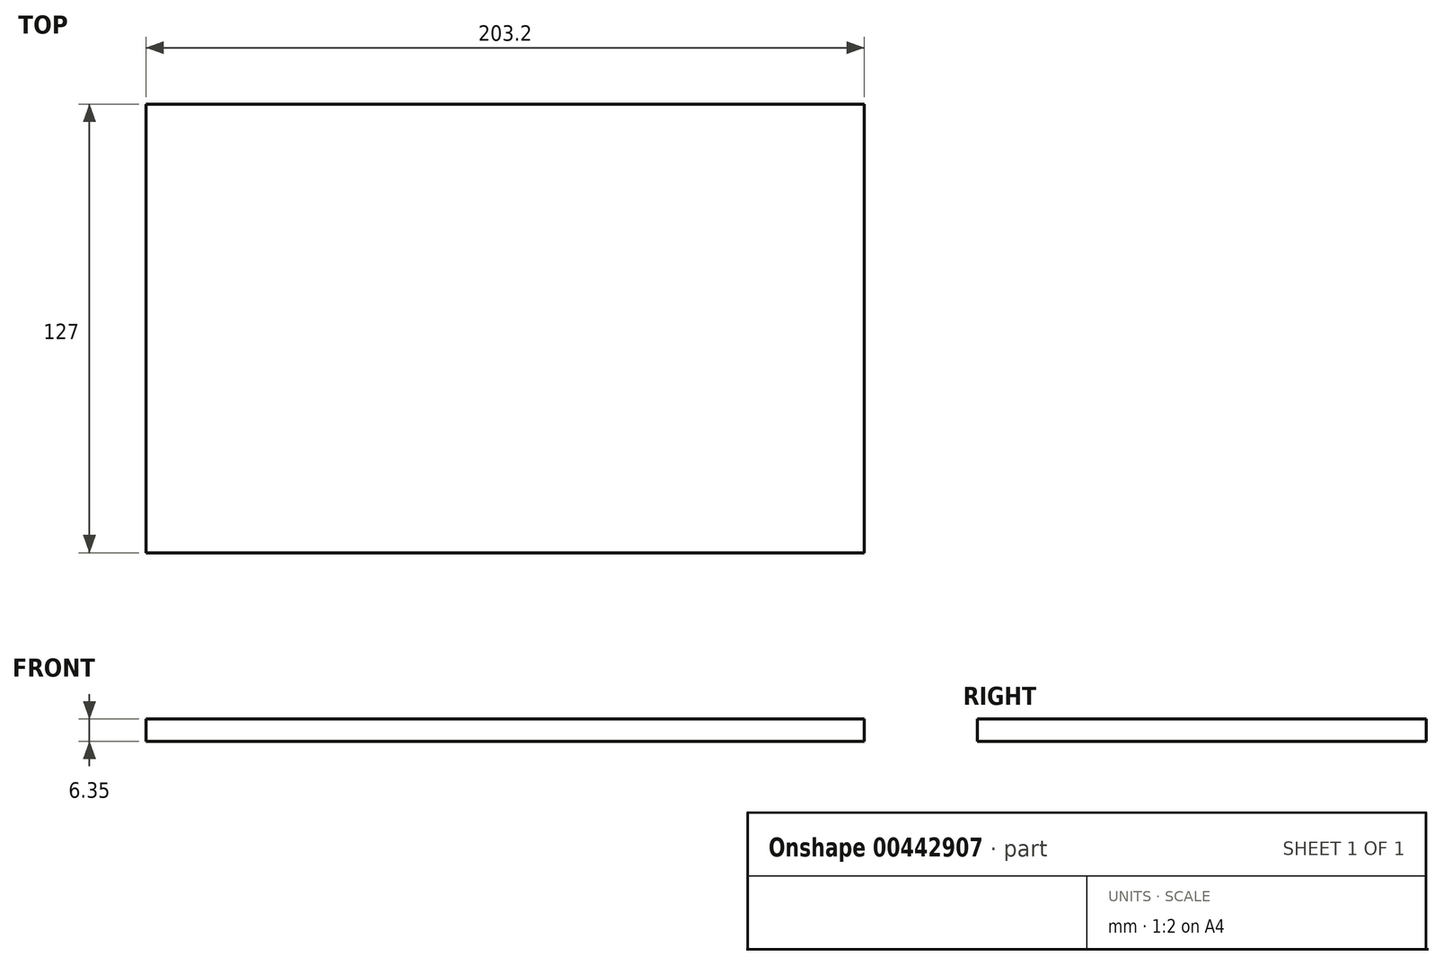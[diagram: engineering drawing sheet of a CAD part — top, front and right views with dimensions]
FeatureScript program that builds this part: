
annotation { "Feature Type Name" : "Feature", "Feature Type Description" : "" }
export const myFeature = defineFeature(function(context is Context, id is Id, definition is map)
    precondition{}
    {
        {
            var Q0;
            Q0=qCreatedBy(makeId("Top.planeOp"),FACE);
            var sketch = newSketch(context, id + "F0", { "sketchPlane" : qUnion([Q0])});
            skLineSegment(sketch, "E0.bottom", {"start": v(101.6, 63.5) * mm, "end": v(-101.6, 63.5) * mm});
            skLineSegment(sketch, "E0.top", {"start": v(101.6, -63.5) * mm, "end": v(-101.6, -63.5) * mm});
            skLineSegment(sketch, "E0.left", {"start": v(101.6, 63.5) * mm, "end": v(101.6, -63.5) * mm});
            skLineSegment(sketch, "E0.right", {"start": v(-101.6, 63.5) * mm, "end": v(-101.6, -63.5) * mm});
            skPoint(sketch, "E0.middle", {"position": v(0, 0) * mm});
            skSolve(sketch);
        }
        {
            var Q0;
            Q0 = qSketchRegion(id + "F0", true);
            extrude(context, id + "F1", {"entities" : qUnion([Q0]), "depth" : 6.35 * mm});
        }
    });
